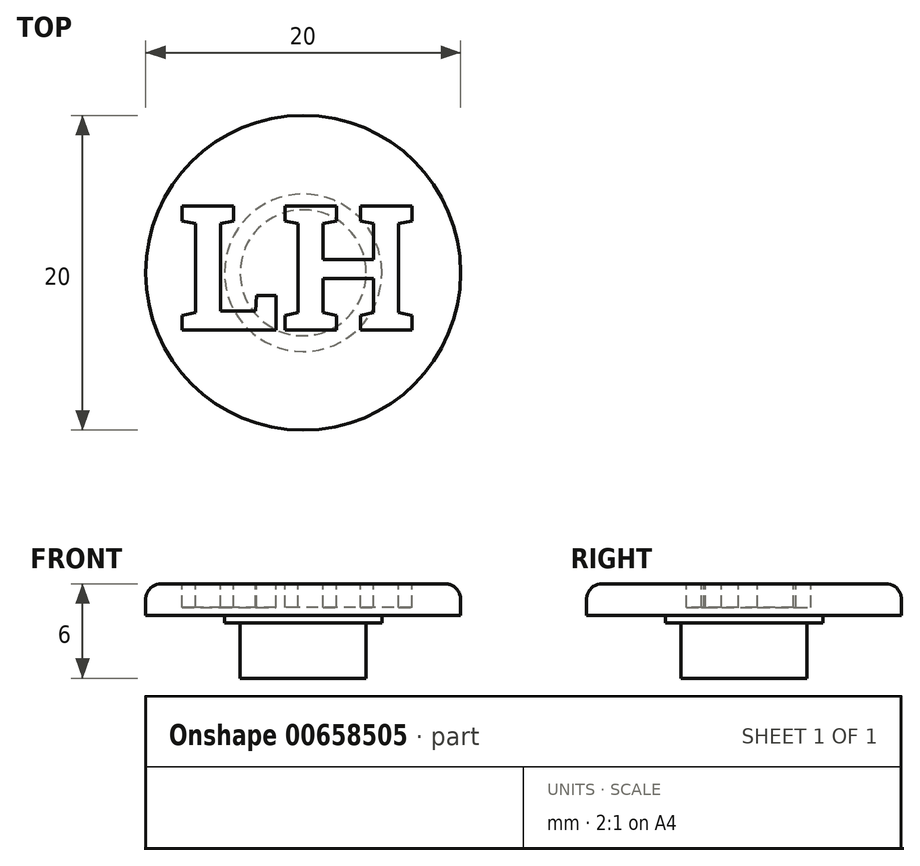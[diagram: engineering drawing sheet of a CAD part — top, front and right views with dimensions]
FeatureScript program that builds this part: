
annotation { "Feature Type Name" : "Feature", "Feature Type Description" : "" }
export const myFeature = defineFeature(function(context is Context, id is Id, definition is map)
    precondition{}
    {
        {
            var Q0;
            Q0=qCreatedBy(makeId("Top.planeOp"),FACE);
            var sketch = newSketch(context, id + "F0", { "sketchPlane" : qUnion([Q0])});
            skCircle(sketch, "E0", {"center": v(0, 0) * mm, "radius": 10 * mm});
            skCircle(sketch, "E1", {"center": v(0, 0) * mm, "radius": 4 * mm});
            skCircle(sketch, "E2", {"center": v(0, 0) * mm, "radius": 5 * mm});
            skSolve(sketch);
        }
        {
            var Q0;
            Q0=makeQuery(id+"F0.imprint","IMPRINT",FACE,{"disambiguationData":[TD([[makeQuery(id+"F0.imprint","IMPRINT",EDGE,{"derivedFrom":sQuery(id+"F0.wireOp",EDGE,"E1")}),1.0]])]});
            extrude(context, id + "F1", {"entities" : qUnion([Q0]), "oppositeDirection" : true, "depth" : 6 * mm, "offsetDistance" : 25 * mm});
        }
        {
            var Q0;
            Q0=makeQuery(id+"F0.imprint","IMPRINT",FACE,{"disambiguationData":[TD([[makeQuery(id+"F0.imprint","IMPRINT",EDGE,{"derivedFrom":sQuery(id+"F0.wireOp",EDGE,"E1")}),-1.0]])]});
            extrude(context, id + "F2", {"entities" : qUnion([Q0]), "operationType" : NewBodyOperationType.ADD, "oppositeDirection" : true, "depth" : 2.5 * mm, "offsetDistance" : 25 * mm});
        }
        {
            var Q0;
            Q0=makeQuery(id+"F0.imprint","IMPRINT",FACE,{"disambiguationData":[TD([[makeQuery(id+"F0.imprint","IMPRINT",EDGE,{"derivedFrom":sQuery(id+"F0.wireOp",EDGE,"E0")}),1.0]])]});
            extrude(context, id + "F3", {"entities" : qUnion([Q0]), "operationType" : NewBodyOperationType.ADD, "oppositeDirection" : true, "depth" : 2 * mm, "offsetDistance" : 25 * mm});
        }
        {
            var Q0;
            Q0=makeQuery(id+"F3.opExtrude","CAP_EDGE",EDGE,{"disambiguationData":[OSD([sQuery(id+"F0.wireOp",EDGE,"E0")])],"isStart":true});
            fillet(context, id + "F4", {"entities" : qUnion([Q0]), "radius" : 1 * mm, "tangentPropagation" : true, "allowEdgeOverflow" : false});
        }
        {
            var Q0;
            Q0=qCreatedBy(makeId("Top.planeOp"),FACE);
            var sketch = newSketch(context, id + "F5", { "sketchPlane" : qUnion([Q0])});
            skText(sketch, "E3", { "text": "LH", "fontName": "RobotoSlab-Bold.ttf"});
            const initialGuessF5  = {"E3": [-0.00798, -0.00365, 1, 0, 0.008]};
            skSetInitialGuess(sketch, initialGuessF5);
            skSolve(sketch);
        }
        {
            var Q0;
            Q0 = qSketchRegion(id + "F5", true);
            extrude(context, id + "F6", {"entities" : qUnion([Q0]), "operationType" : NewBodyOperationType.REMOVE, "oppositeDirection" : true, "depth" : 1.5 * mm, "offsetDistance" : 25 * mm});
        }
    });
